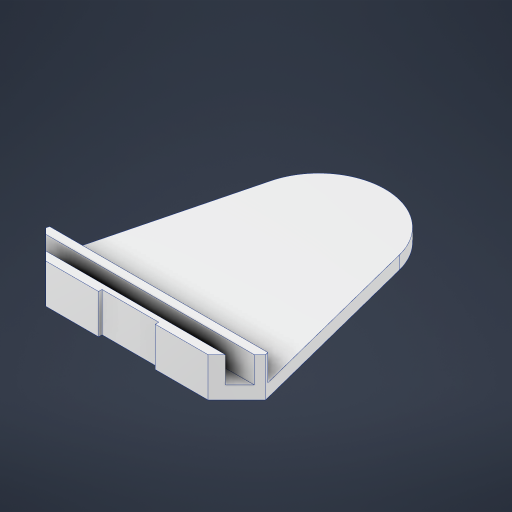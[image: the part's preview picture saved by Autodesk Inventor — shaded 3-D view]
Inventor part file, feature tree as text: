
AUTODESK INVENTOR PART (.ipt)
format: ipt  version: 2024 (Build 280153000, 153)  size: 235,520 bytes
history: native  units: mm
features: extrude x3, sketch x3, chamfer x1, projected_geometry x1
ambient origin geometry x8: Origin, YZ Plane, XZ Plane, XY Plane, X Axis, Y Axis, Z Axis, Center Point
bodies: Solid1 (feature_tree)
feature tree (8):
  extrude  "Extrusion1"  Depth=15.0mm TaperAngle=45.0deg
  chamfer  "Chamfer1"  Distance=16.5mm
  extrude  "Extrusion2"  Depth=30.0mm TaperAngle=0.0deg
  extrude  "Extrusion3"  Depth=65.0mm
  sketch  "Sketch1"  dims[d0=15.0mm d1=0.0mm d2=33.0mm d3=2.0mm d4=45.0deg]
  sketch  "Sketch4"  dims[d5=10.0mm]
  projected_geometry  "Projected Loop2"
  sketch  "Sketch5"  dims[d6=10.0mm d7=16.5mm d8=30.0mm d9=0.0mm d10=65.0mm d11=60.5mm d12=60.5mm d13=4.0mm d14=0.0mm]
